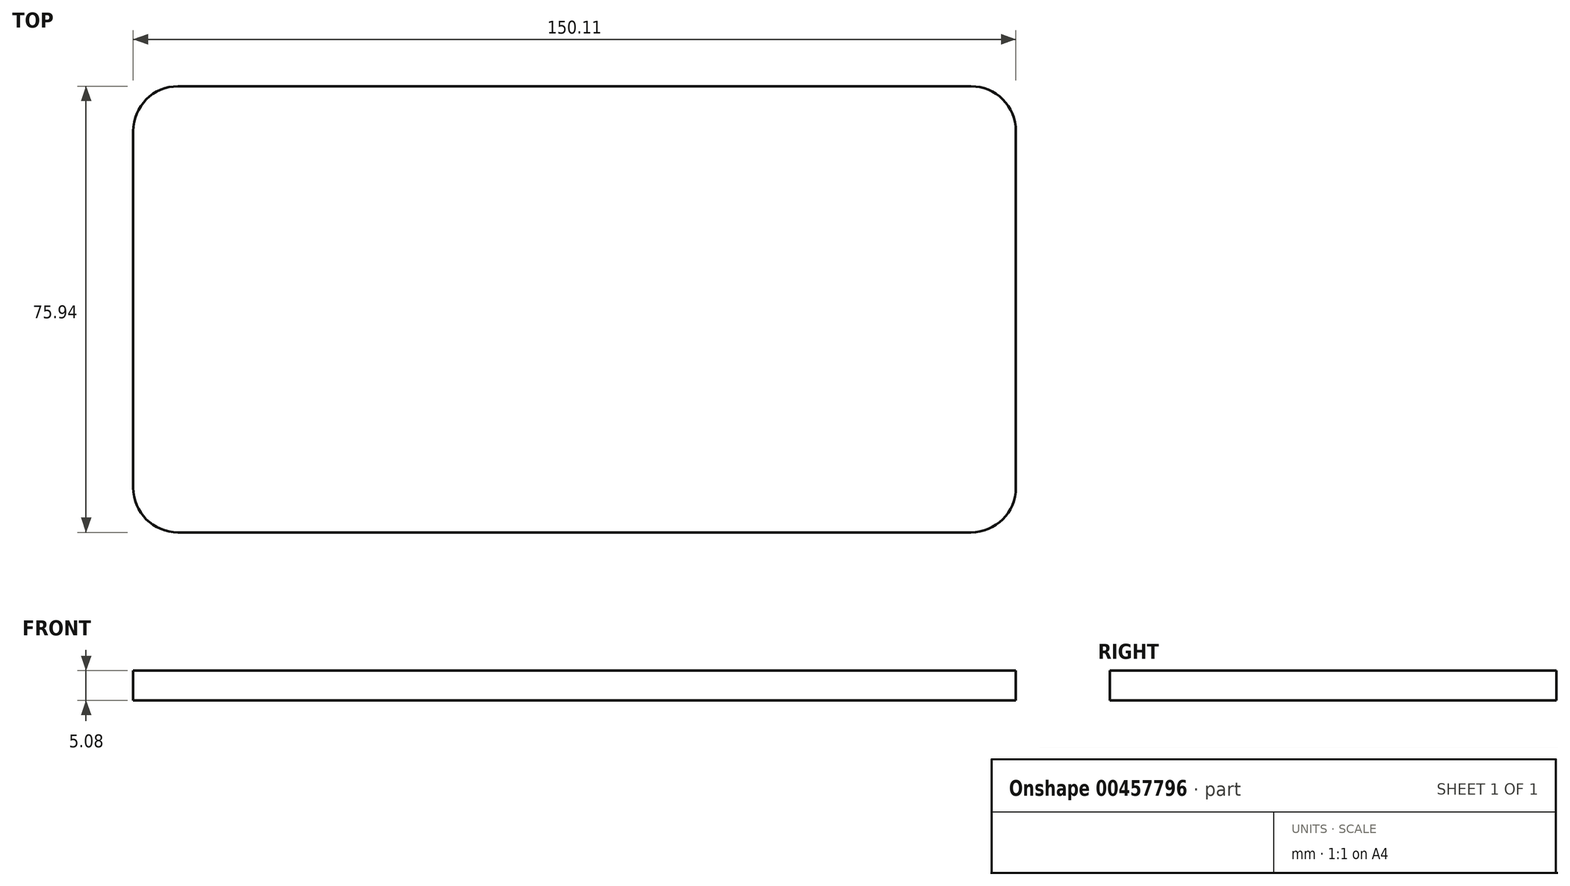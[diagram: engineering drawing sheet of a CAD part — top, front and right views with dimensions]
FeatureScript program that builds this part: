
annotation { "Feature Type Name" : "Feature", "Feature Type Description" : "" }
export const myFeature = defineFeature(function(context is Context, id is Id, definition is map)
    precondition{}
    {
        {
            var Q0;
            Q0=qCreatedBy(makeId("Top.planeOp"),FACE);
            var sketch = newSketch(context, id + "F0", { "sketchPlane" : qUnion([Q0])});
            skLineSegment(sketch, "E0.bottom", {"start": v(-118.04, 52.7) * mm, "end": v(32.07, 52.7) * mm});
            skLineSegment(sketch, "E0.top", {"start": v(-118.04, -23.24) * mm, "end": v(32.07, -23.24) * mm});
            skLineSegment(sketch, "E0.left", {"start": v(-118.04, 52.7) * mm, "end": v(-118.04, -23.24) * mm});
            skLineSegment(sketch, "E0.right", {"start": v(32.07, 52.7) * mm, "end": v(32.07, -23.24) * mm});
            skSolve(sketch);
        }
        {
            var Q0;
            Q0=makeQuery(id+"F0.imprint","IMPRINT",FACE,{"disambiguationData":[TD([[makeQuery(id+"F0.imprint","IMPRINT",EDGE,{"derivedFrom":sQuery(id+"F0.wireOp",EDGE,"E0.bottom")}),-1.0]])]});
            extrude(context, id + "F1", {"entities" : qUnion([Q0]), "depth" : 5.08 * mm});
        }
        {
            var Q0;
            Q0=makeQuery(id+"F1.opExtrude","SWEPT_EDGE",EDGE,{"disambiguationData":[OSD([sQuery(id+"F0.wireOp",EDGE,"E0.top"),sQuery(id+"F0.wireOp",EDGE,"E0.left")])]});
            var Q1;
            Q1=makeQuery(id+"F1.opExtrude","SWEPT_EDGE",EDGE,{"disambiguationData":[OSD([sQuery(id+"F0.wireOp",EDGE,"E0.top"),sQuery(id+"F0.wireOp",EDGE,"E0.right")])]});
            var Q2;
            Q2=makeQuery(id+"F1.opExtrude","SWEPT_EDGE",EDGE,{"disambiguationData":[OSD([sQuery(id+"F0.wireOp",EDGE,"E0.bottom"),sQuery(id+"F0.wireOp",EDGE,"E0.right")])]});
            var Q3;
            Q3=makeQuery(id+"F1.opExtrude","SWEPT_EDGE",EDGE,{"disambiguationData":[OSD([sQuery(id+"F0.wireOp",EDGE,"E0.bottom"),sQuery(id+"F0.wireOp",EDGE,"E0.left")])]});
            fillet(context, id + "F2", {"entities" : qUnion([Q0, Q1, Q2, Q3]), "radius" : 7.62 * mm, "tangentPropagation" : true, "allowEdgeOverflow" : false});
        }
        {
            var Q0;
            Q0=makeQuery(id+"F1.opExtrude","CAP_FACE",FACE,{"disambiguationData":[OSD([sQuery(id+"F0.wireOp",EDGE,"E0.bottom"),sQuery(id+"F0.wireOp",EDGE,"E0.top"),sQuery(id+"F0.wireOp",EDGE,"E0.left"),sQuery(id+"F0.wireOp",EDGE,"E0.right")])],"isStart":false});
            extrude(context, id + "F3", {"entities" : qUnion([Q0]), "operationType" : NewBodyOperationType.ADD, "depth" : -2.54 * mm});
        }
        {
            var Q0;
            Q0=makeQuery(id+"F1.opExtrude","CAP_FACE",FACE,{"disambiguationData":[OSD([sQuery(id+"F0.wireOp",EDGE,"E0.bottom"),sQuery(id+"F0.wireOp",EDGE,"E0.top"),sQuery(id+"F0.wireOp",EDGE,"E0.left"),sQuery(id+"F0.wireOp",EDGE,"E0.right")])],"isStart":false});
            extrude(context, id + "F4", {"entities" : qUnion([Q0]), "operationType" : NewBodyOperationType.ADD, "depth" : -2.54 * mm});
        }
        {
            var Q0;
            Q0=makeQuery(id+"F1.opExtrude","CAP_FACE",FACE,{"disambiguationData":[OSD([sQuery(id+"F0.wireOp",EDGE,"E0.bottom"),sQuery(id+"F0.wireOp",EDGE,"E0.top"),sQuery(id+"F0.wireOp",EDGE,"E0.left"),sQuery(id+"F0.wireOp",EDGE,"E0.right")])],"isStart":true});
            extrude(context, id + "F5", {"entities" : qUnion([Q0]), "operationType" : NewBodyOperationType.ADD, "depth" : -5.08 * mm});
        }
    });
